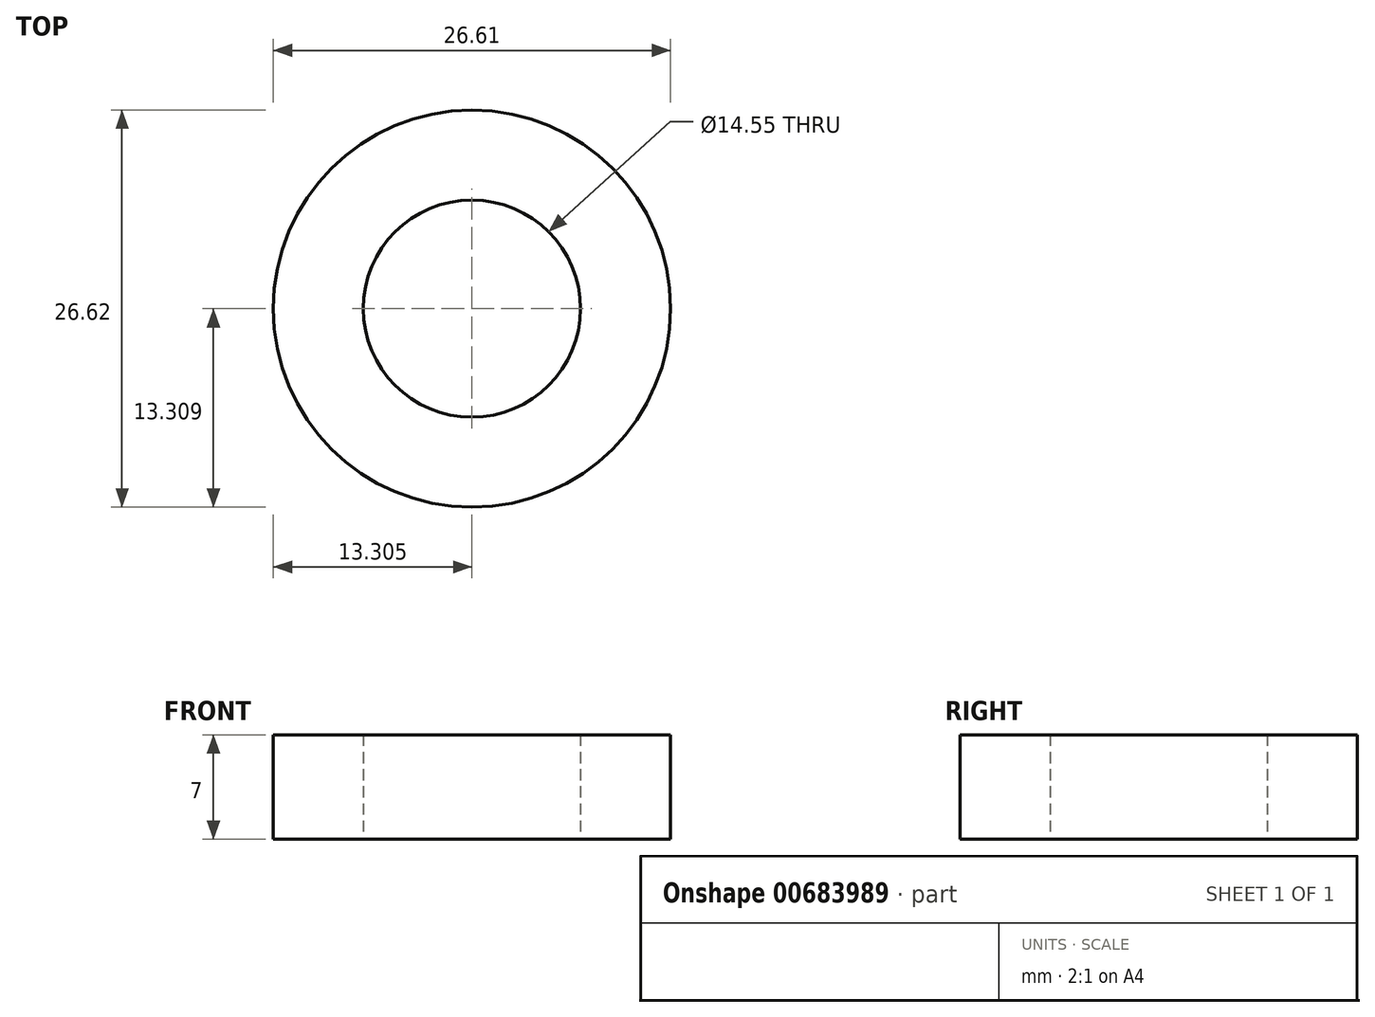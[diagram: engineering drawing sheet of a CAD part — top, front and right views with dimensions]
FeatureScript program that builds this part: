
annotation { "Feature Type Name" : "Feature", "Feature Type Description" : "" }
export const myFeature = defineFeature(function(context is Context, id is Id, definition is map)
    precondition{}
    {
        {
            var Q0;
            Q0=qCreatedBy(makeId("Top.planeOp"),FACE);
            var sketch = newSketch(context, id + "F0", { "sketchPlane" : qUnion([Q0])});
            skCircle(sketch, "E0", {"center": v(-4.59, 5.65) * mm, "radius": 13.3 * mm});
            skCircle(sketch, "E1", {"center": v(-4.59, 5.65) * mm, "radius": 7.28 * mm});
            skSolve(sketch);
        }
        {
            var Q0;
            Q0=makeQuery(id+"F0.imprint","IMPRINT",FACE,{"disambiguationData":[TD([[makeQuery(id+"F0.imprint","IMPRINT",EDGE,{"derivedFrom":sQuery(id+"F0.wireOp",EDGE,"E0")}),1.0]])]});
            extrude(context, id + "F1", {"entities" : qUnion([Q0]), "depth" : 7 * mm, "offsetDistance" : 25.4 * mm});
        }
    });
